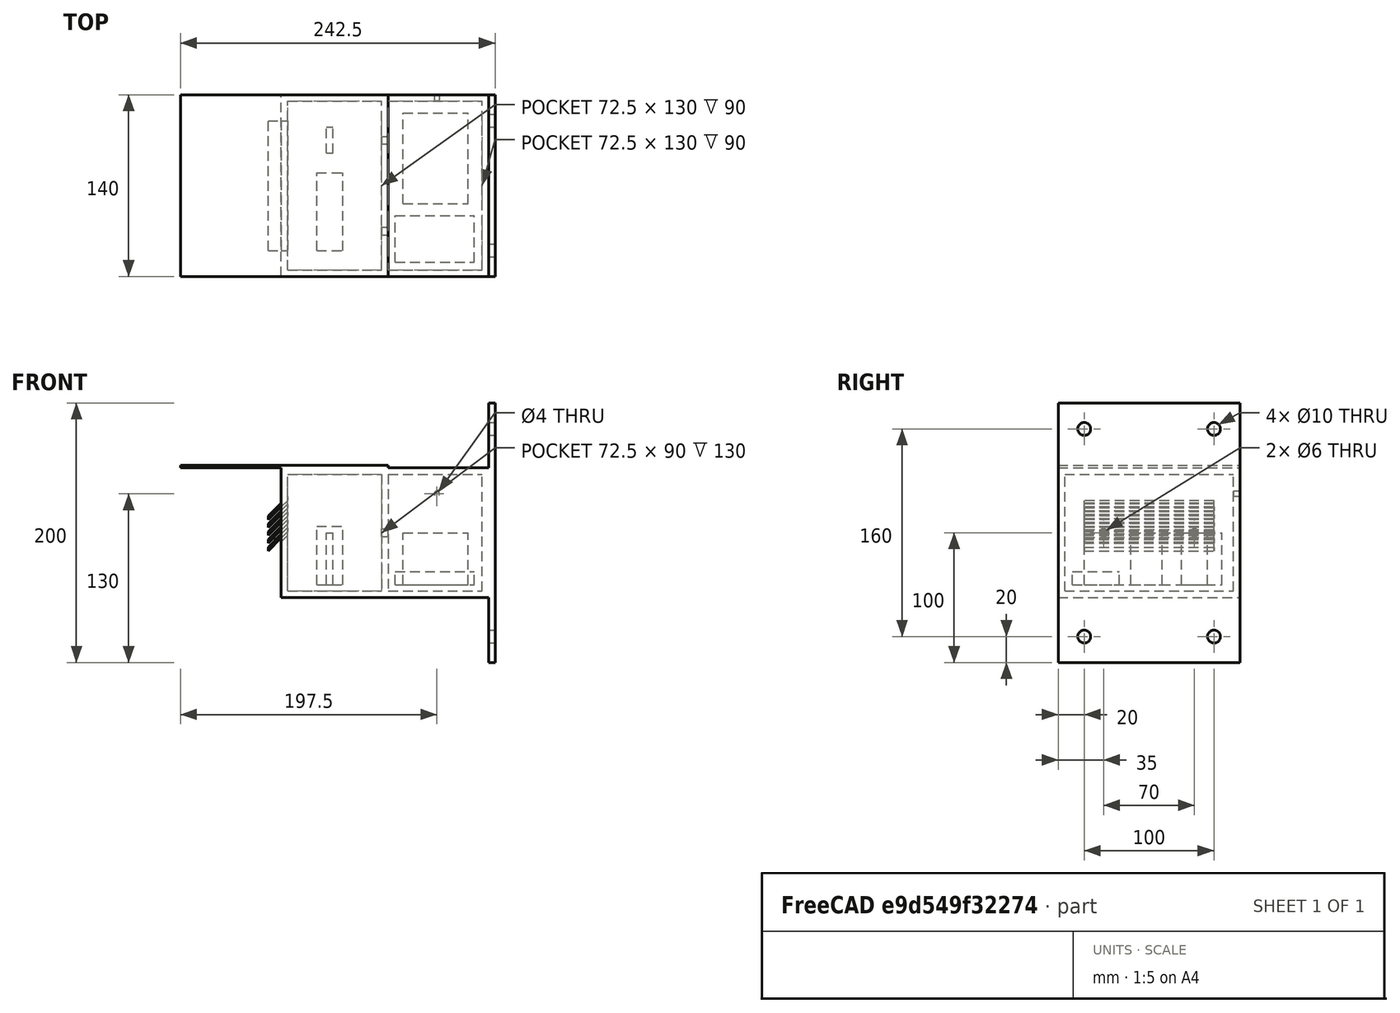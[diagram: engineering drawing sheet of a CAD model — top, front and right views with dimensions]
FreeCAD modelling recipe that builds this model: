
FCSTD DOCUMENT  (FreeCAD 0.17R13541 (Git))
Label: ParticulateSensor
License: All rights reserved
LicenseURL: http://en.wikipedia.org/wiki/All_rights_reserved
objects: Part::Box×18, Part::Cut×14, Part::Cylinder×7, Part::MultiFuse×7, PartDesign::FeatureBase×1, PartDesign::Body×1
note: 48 computed .brp shape members not serialized (recipe doc carries the construction recipe); baked Part::Feature solids carry a one-line shape summary decoded from their .brp

FEATURE [PartDesign::FeatureBase] BaseFeature001
FEATURE [PartDesign::Body] Body001
  Group = -> [BaseFeature001]
  Origin = -> Origin001
  Tip = -> BaseFeature001
FEATURE [Part::Cylinder] Cylinder
  Angle = 360
  AttacherType = Attacher::AttachEngine3D
  Height = 10
  Placement = pos=(160,20,130) rot=(0,1,0;1.5708rad)
  Radius = 5
FEATURE [Part::Cylinder] Cylinder001
  Angle = 360
  AttacherType = Attacher::AttachEngine3D
  Height = 10
  Placement = pos=(160,120,130) rot=(0,1,0;1.5708rad)
  Radius = 5
FEATURE [Part::Cylinder] Cylinder002
  Angle = 360
  AttacherType = Attacher::AttachEngine3D
  Height = 10
  Placement = pos=(160,20,-30) rot=(0,1,0;1.5708rad)
  Radius = 5
FEATURE [Part::Cylinder] Cylinder003
  Angle = 360
  AttacherType = Attacher::AttachEngine3D
  Height = 10
  Placement = pos=(160,120,-30) rot=(0,1,0;1.5708rad)
  Radius = 5
FEATURE [Part::Cut] Cut
  Base = -> Body001
  Tool = -> Cylinder002
FEATURE [Part::Cut] Cut001
  Base = -> Cut
  Tool = -> Cylinder003
FEATURE [Part::Cut] Cut002
  Base = -> Cut001
  Tool = -> Cylinder
FEATURE [Part::Cut] Cut003
  Base = -> Cut002
  Tool = -> Cylinder001
FEATURE [Part::Box] Box  label="Cube"
  AttacherType = Attacher::AttachEngine3D
  Height = 100
  Length = 5
  Placement = pos=(77.5,0,0) rot=(0,0,1;0rad)
  Width = 140
FEATURE [Part::MultiFuse] Fusion
  Shapes = -> [Cut003,Box]
FEATURE [Part::Cylinder] Cylinder004
  Angle = 360
  AttacherType = Attacher::AttachEngine3D
  Height = 10
  Placement = pos=(77,35,50) rot=(0,1,0;1.5708rad)
  Radius = 3
FEATURE [Part::Cylinder] Cylinder005
  Angle = 360
  AttacherType = Attacher::AttachEngine3D
  Height = 10
  Placement = pos=(77,105,50) rot=(0,1,0;1.5708rad)
  Radius = 3
FEATURE [Part::Cut] Cut004
  Base = -> Fusion
  Tool = -> Cylinder004
FEATURE [Part::Cut] Cut005
  Base = -> Cut004
  Tool = -> Cylinder005
FEATURE [Part::Box] Box001  label="Cube001"
  AttacherType = Attacher::AttachEngine3D
  Height = 2
  Length = 160
  Placement = pos=(-77.5,0,100) rot=(0,0,1;0rad)
  Width = 140
FEATURE [Part::Cylinder] Cylinder006
  Angle = 360
  AttacherType = Attacher::AttachEngine3D
  Height = 20
  Placement = pos=(120,150,80) rot=(1,0,0;1.5708rad)
  Radius = 2
FEATURE [Part::MultiFuse] Fusion001
  Shapes = -> [Box001,Cut005]
FEATURE [Part::Cut] Cut006
  Base = -> Fusion001
  Tool = -> Cylinder006
FEATURE [Part::Box] Box007  label="Cube007"
  AttacherType = Attacher::AttachEngine3D
  Height = 2
  Length = 25
  Placement = pos=(-10,20,60) rot=(0,-1,0;0.785398rad)
  Width = 100
FEATURE [Part::Box] Box008  label="Cube008"
  AttacherType = Attacher::AttachEngine3D
  Height = 2
  Length = 25
  Placement = pos=(-10,20,57) rot=(0,-1,0;0.785398rad)
  Width = 100
FEATURE [Part::Box] Box009  label="Cube009"
  AttacherType = Attacher::AttachEngine3D
  Height = 2
  Length = 25
  Placement = pos=(-10,20,54) rot=(0,-1,0;0.785398rad)
  Width = 100
FEATURE [Part::Box] Box010  label="Cube010"
  AttacherType = Attacher::AttachEngine3D
  Height = 2
  Length = 25
  Placement = pos=(-10,20,51) rot=(0,-1,0;0.785398rad)
  Width = 100
FEATURE [Part::Box] Box011  label="Cube011"
  AttacherType = Attacher::AttachEngine3D
  Height = 2
  Length = 25
  Placement = pos=(-10,20,48) rot=(0,-1,0;0.785398rad)
  Width = 100
FEATURE [Part::Box] Box012  label="Cube012"
  AttacherType = Attacher::AttachEngine3D
  Height = 2
  Length = 25
  Placement = pos=(-10,20,45) rot=(0,-1,0;0.785398rad)
  Width = 100
FEATURE [Part::Box] Box013  label="Cube013"
  AttacherType = Attacher::AttachEngine3D
  Height = 2
  Length = 25
  Placement = pos=(-10,20,42) rot=(0,-1,0;0.785398rad)
  Width = 100
FEATURE [Part::Box] Box014  label="Cube014"
  AttacherType = Attacher::AttachEngine3D
  Height = 2
  Length = 25
  Placement = pos=(-10,20,39) rot=(0,-1,0;0.785398rad)
  Width = 100
FEATURE [Part::Box] Box015  label="Cube015"
  AttacherType = Attacher::AttachEngine3D
  Height = 2
  Length = 25
  Placement = pos=(-10,20,36) rot=(0,-1,0;0.785398rad)
  Width = 100
FEATURE [Part::Box] Box016  label="Cube016"
  AttacherType = Attacher::AttachEngine3D
  Height = 2
  Length = 25
  Placement = pos=(-10,20,33) rot=(0,-1,0;0.785398rad)
  Width = 100
FEATURE [Part::Cut] Cut007
  Base = -> Cut006
  Tool = -> Box008
FEATURE [Part::Cut] Cut008
  Base = -> Cut007
  Tool = -> Box016
FEATURE [Part::Cut] Cut009
  Base = -> Cut008
  Tool = -> Box014
FEATURE [Part::Cut] Cut010
  Base = -> Cut009
  Tool = -> Box012
FEATURE [Part::Cut] Cut011
  Base = -> Cut010
  Tool = -> Box010
FEATURE [Part::Box] Box017  label="Cube017"
  AttacherType = Attacher::AttachEngine3D
  Height = 80
  Length = 10
  Placement = pos=(-20,0,0) rot=(0,0,1;0rad)
  Width = 140
FEATURE [Part::MultiFuse] Fusion002
  Shapes = -> [Box015,Box013,Box007,Box011,Box009,Cut011]
FEATURE [Part::Cut] Cut012
  Base = -> Fusion002
  Tool = -> Box017
FEATURE [Part::Box] Box018  label="Cube018"
  AttacherType = Attacher::AttachEngine3D
  Height = 82
  Length = 10
  Placement = pos=(5,16,8) rot=(0,0,1;0rad)
  Width = 110
FEATURE [Part::Cut] Cut013
  Base = -> Cut012
  Tool = -> Box018
FEATURE [Part::Box] Box019  label="Cube019"
  AttacherType = Attacher::AttachEngine3D
  Height = 40
  Length = 5
  Placement = pos=(35,95,10) rot=(0,0,1;0rad)
  Width = 20
  expr: Length = 5
FEATURE [Part::MultiFuse] Fusion003
  Shapes = -> [Box019,Cut013]
FEATURE [Part::Box] Box020  label="Cube020"
  AttacherType = Attacher::AttachEngine3D
  Height = 45
  Length = 20
  Placement = pos=(27.5,20,10) rot=(0,0,1;0rad)
  Width = 60
FEATURE [Part::Box] Box021  label="Cube021"
  AttacherType = Attacher::AttachEngine3D
  Height = 40
  Length = 50
  Placement = pos=(94,56,10) rot=(0,0,1;0rad)
  Width = 70
FEATURE [Part::MultiFuse] Fusion004
  Shapes = -> [Box020,Fusion003]
FEATURE [Part::Box] Box022  label="Cube022"
  AttacherType = Attacher::AttachEngine3D
  Height = 10
  Length = 61
  Placement = pos=(88,11,10) rot=(0,0,1;0rad)
  Width = 36
FEATURE [Part::MultiFuse] Fusion005
  Shapes = -> [Box022,Fusion004]
FEATURE [Part::MultiFuse] Fusion006
  Shapes = -> [Fusion005,Box021]
